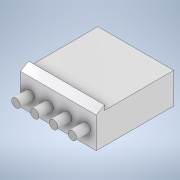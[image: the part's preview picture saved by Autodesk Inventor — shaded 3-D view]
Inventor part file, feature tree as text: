
AUTODESK INVENTOR PART (.ipt)
format: ipt  version: 2020 (Build 240168000, 168)  size: 143,872 bytes
history: native  units: mm
features: extrude x3, sketch x3, projected_geometry x2, other x1
ambient origin geometry x8: Origin, YZ Plane, XZ Plane, XY Plane, X Axis, Y Axis, Z Axis, Center Point
bodies: Body1 (feature_tree)
feature tree (9):
  other  "Sólido1"
  extrude  "Extrusión1"  Depth=16.0mm
  extrude  "Extrusión2"  Depth=8.175mm
  extrude  "Extrusión3"  Depth=3.0mm
  sketch  "Boceto1"  dims[d0=16.35mm d1=16.0mm]
  sketch  "Boceto2"  dims[d2=8.0mm d3=8.175mm]
  projected_geometry  "Contorno proyectado1"
  sketch  "Boceto3"  dims[d4=6.5mm d5=0.0mm d6=7.5mm d7=60.0deg d8=16.0mm d9=0.0mm d10=3.25mm d12=3.96mm d13=3.96mm d14=2.06mm d15=1.8mm d16=1.8mm d17=1.8mm d18=1.8mm d19=3.0mm d20=0.0mm]
  projected_geometry  "Contorno proyectado2"
